# Revit family: Lectrus Boiler KEB0015-0150
name_source: partatom
category: Mechanical Equipment
units: mm (PartAtom-declared; Revit-internal decimal feet)

## family parameters
Always vertical = Yes
Cut with Voids When Loaded = No
OmniClass Number = 23.65.35.11.17
OmniClass Title = Thermodynamic Water Heaters
Part Type = Normal
Room Calculation Point = No
Round Connector Dimension = Use Radius
Shared = No
Work Plane-Based = No

## types (10) — shared parameters
Bottom of Box = 14"
Clearance Visibility = Yes
Description = Lectrus Commercial Electric Boiler
E_Box Depth = 6 1/4"
F_Water Outlet Offset = 3 1/4"
Front Clearance = 36"
G_Water Outlet Height = 39 3/4"
HEIGHT = 47"
H_Water Inlet Height = 9"
Left Clearance = 3"
Manufacturer = Lochinvar
Rear Clearance = 36"
Right Clearance = 3"
SES BIM Studio # = 24 0649 01
Top Clearance = 32"
WATER INLET SIZE = 2"
WATER OUTLET SIZE = 2"
Water Inlet Radius = 1"
Water Outlet Radius = 1"

## per-type parameters (varying)
| type | 208V-3PH FLA | 208V-3PH MCA | 240V-1PH FLA | 240V-1PH MCA | 480V-3PH FLA | 480V-3PH MCA | 600V-3PH FLA | 600V-3PH MCA | BTU/H HEATING | DEPTH | D_Unit Depth | Element Quantity | GALLON CAPACITY | J_Drain Height | KW | K_Water Inlet Offset | L_Drain Offset | M_Top of Box | WIDTH |
| KEB0015 | 44 | 55 | 66 | 83 | 19 | 24 | 15 | 19 | 51,180 | 41" | 30 1/4" | 1 | 17 | 1 3/4" | 15 | 3 1/4" | 8 1/2" | 40 3/4" | 16 3/4" |
| KEB0030 | 88 | 110 | 132 | 165 | 38 | 48 | 30 | 38 | 102,360 | 41" | 30 1/4" | 2 | 17 | 1 3/4" | 30 | 3 1/4" | 8 1/2" | 40 3/4" | 16 3/4" |
| KEB0045 | 131 | 165 |  |  | 57 | 72 | 46 | 57 | 153,540 | 41" | 30 1/4" | 3 | 17 | 1 3/4" | 45 | 3 1/4" | 8 1/2" | 40 3/4" | 16 3/4" |
| KEB0060 | 175 | 220 |  |  | 76 | 95 | 61 | 76 | 204,720 | 41" | 30 1/4" | 4 | 17 | 1 3/4" | 60 | 3 1/4" | 8 1/2" | 40 3/4" | 16 3/4" |
| KEB0075 | 219 | 274 |  |  | 95 | 119 | 76 | 95 | 255,900 | 41" | 30 1/4" | 5 | 17 | 1 3/4" | 75 | 3 1/4" | 8 1/2" | 40 3/4" | 16 3/4" |
| KEB0090 | 263 | 329 |  |  | 114 | 143 | 91 | 114 | 307,080 | 41" | 30 1/4" | 6 | 17 | 1 3/4" | 90 | 3 1/4" | 8 1/2" | 40 3/4" | 16 3/4" |
| KEB0105 | 307 | 384 |  |  | 133 | 167 | 106 | 133 | 358,260 | 45 1/4" | 35 1/2" | 7 | 32 | 2 1/4" | 105 | 4 1/4" | 11 1/4" | 41 1/4" | 21 3/4" |
| KEB0120 | 351 | 439 |  |  | 152 | 190 | 122 | 152 | 409,440 | 45 1/4" | 35 1/2" | 8 | 32 | 2 1/4" | 120 | 4 1/4" | 11 1/4" | 41 1/4" | 21 3/4" |
| KEB0135 | 394 | 494 |  |  | 171 | 214 | 137 | 171 | 460,620 | 45 1/4" | 35 1/2" | 9 | 32 | 2 1/4" | 135 | 4 1/4" | 11 1/4" | 41 1/4" | 21 3/4" |
| KEB0150 | 438 | 548 |  |  | 190 | 238 | 152 | 190 | 511,800 | 45 1/4" | 35 1/2" | 10 | 32 | 2 1/4" | 150 | 4 1/4" | 11 1/4" | 41 1/4" | 21 3/4" |

note: column(s) folded — value = type name in every type: MODEL NO., Model

## geometry (parser evidence)
native form markers: Sweep x2
no freeform markers — native parametric forms only
